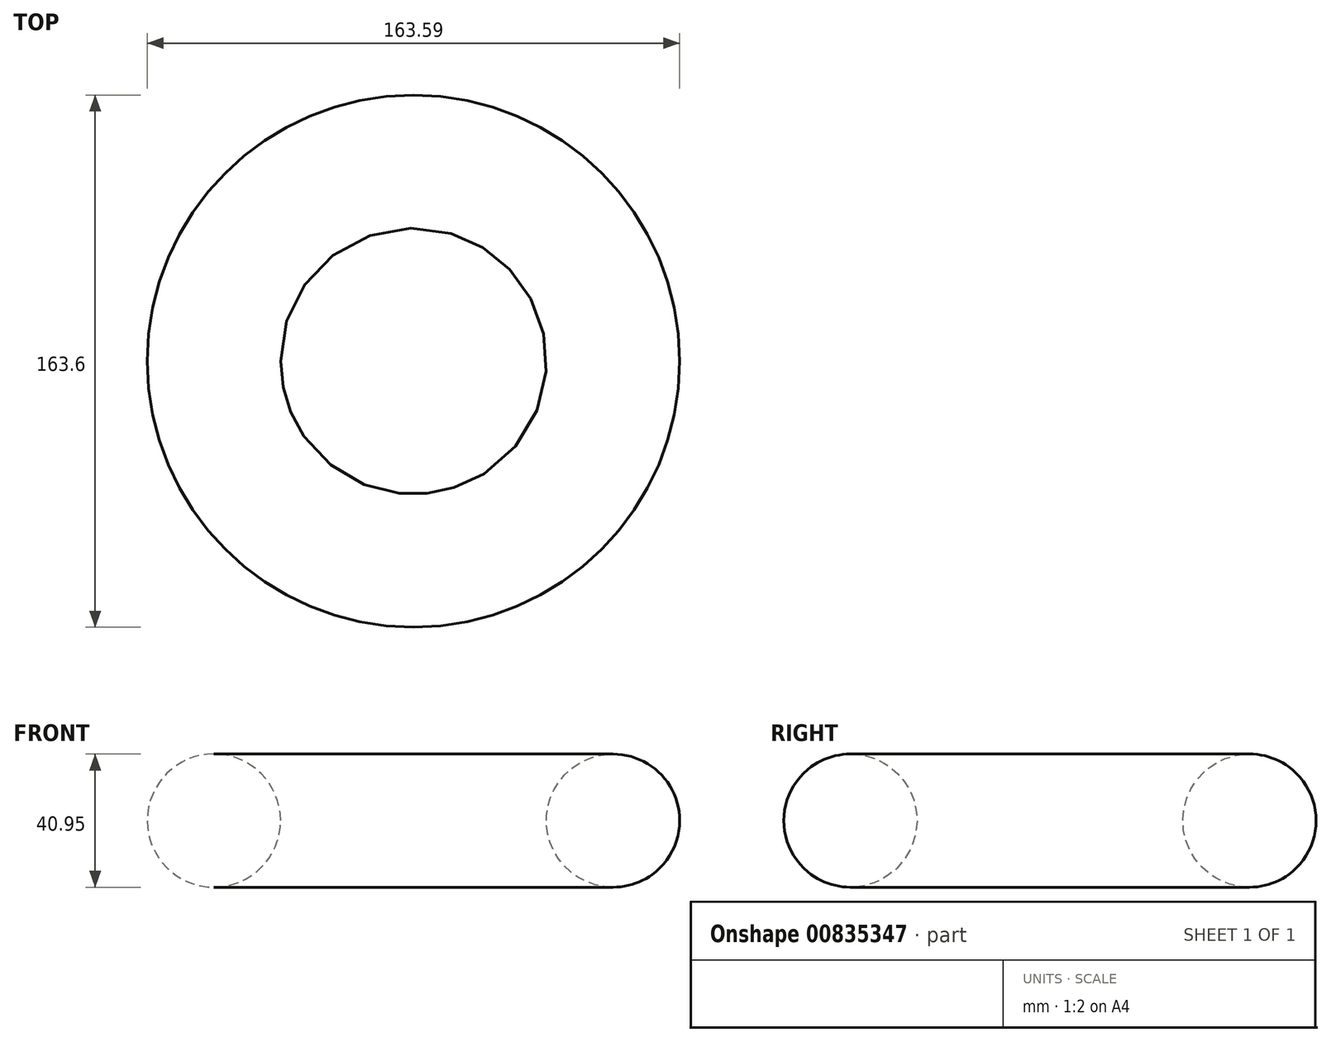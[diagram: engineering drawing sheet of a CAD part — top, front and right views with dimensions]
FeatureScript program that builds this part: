
annotation { "Feature Type Name" : "Feature", "Feature Type Description" : "" }
export const myFeature = defineFeature(function(context is Context, id is Id, definition is map)
    precondition{}
    {
        {
            var Q0;
            Q0=qCreatedBy(makeId("Front.planeOp"),FACE);
            var sketch = newSketch(context, id + "F0", { "sketchPlane" : qUnion([Q0])});
            skLineSegment(sketch, "E0", {"start": v(-24.97, 52.42) * mm, "end": v(-24.97, -15.33) * mm, "construction": true});
            skCircle(sketch, "E1", {"center": v(36.35, -28.18) * mm, "radius": 20.47 * mm});
            skCircle(sketch, "E2", {"center": v(36.35, -28.18) * mm, "radius": 10.24 * mm});
            skSolve(sketch);
        }
        {
            var Q0;
            Q0=sQuery(id+"F0.wireOp",EDGE,"E1");
            var Q1;
            Q1=sQuery(id+"F0.wireOp",EDGE,"E0");
            revolve(context, id + "F1", {"bodyType" : ToolBodyType.SURFACE, "surfaceOperationType" : NewSurfaceOperationType.NEW, "surfaceEntities" : qUnion([Q0]), "axis" : qUnion([Q1]), "revolveType" : RevolveType.FULL});
        }
    });
